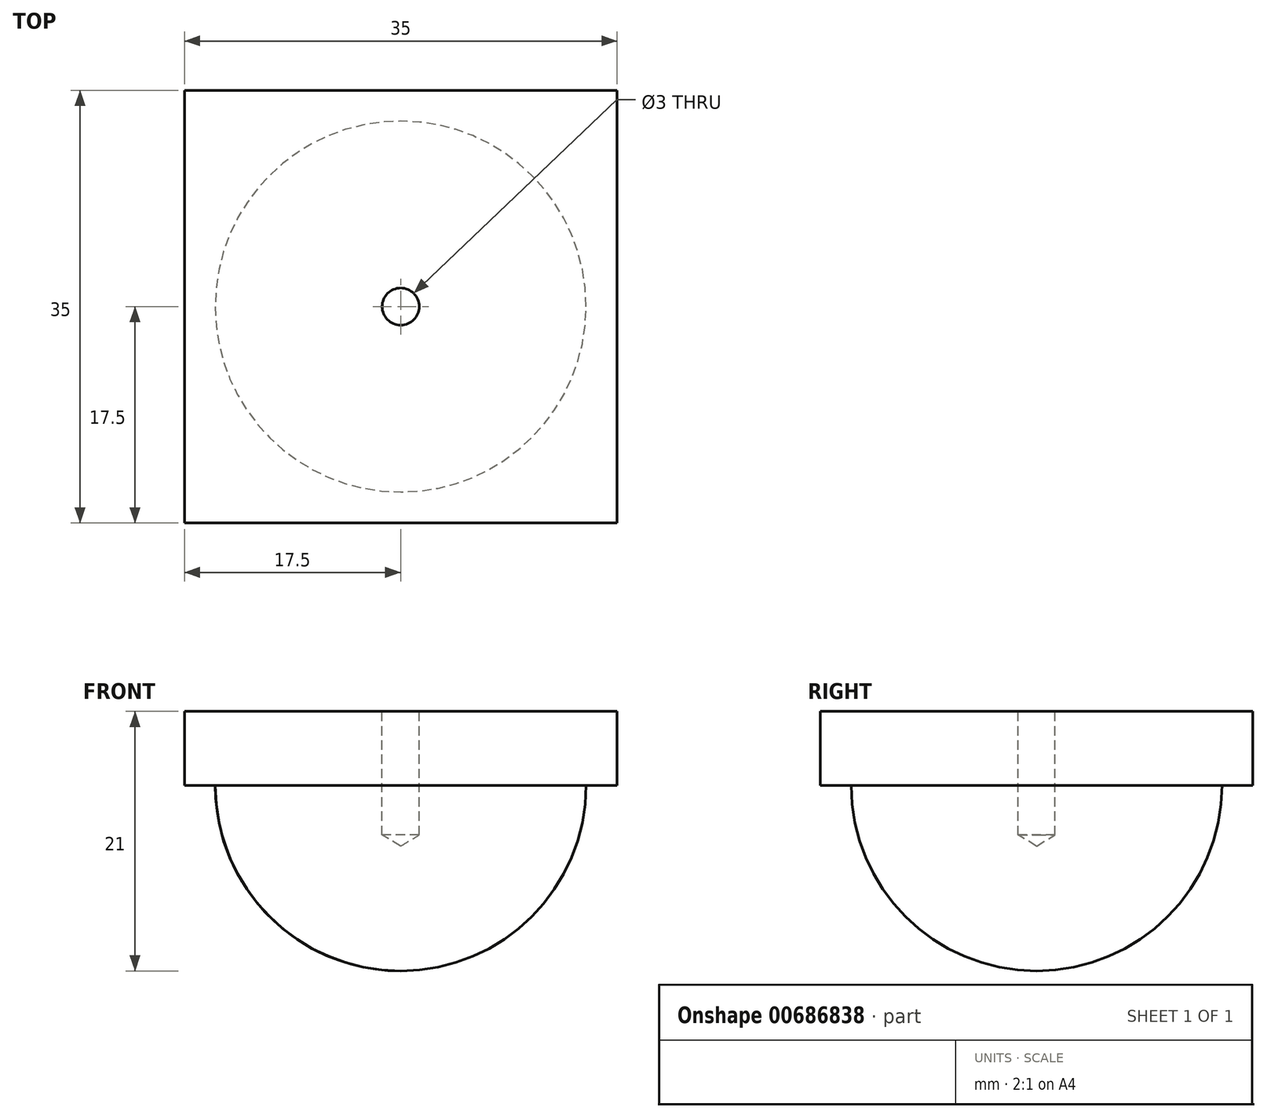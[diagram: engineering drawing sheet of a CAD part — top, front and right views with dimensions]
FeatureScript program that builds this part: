
annotation { "Feature Type Name" : "Feature", "Feature Type Description" : "" }
export const myFeature = defineFeature(function(context is Context, id is Id, definition is map)
    precondition{}
    {
        {
            var Q0;
            Q0=qCreatedBy(makeId("Top.planeOp"),FACE);
            var sketch = newSketch(context, id + "F0", { "sketchPlane" : qUnion([Q0])});
            skLineSegment(sketch, "E0.bottom", {"start": v(-17.5, -17.5) * mm, "end": v(17.5, -17.5) * mm});
            skLineSegment(sketch, "E0.top", {"start": v(-17.5, 17.5) * mm, "end": v(17.5, 17.5) * mm});
            skLineSegment(sketch, "E0.left", {"start": v(-17.5, -17.5) * mm, "end": v(-17.5, 17.5) * mm});
            skLineSegment(sketch, "E0.right", {"start": v(17.5, -17.5) * mm, "end": v(17.5, 17.5) * mm});
            skPoint(sketch, "E0.middle", {"position": v(0, 0) * mm});
            skSolve(sketch);
        }
        {
            var Q0;
            Q0 = qSketchRegion(id + "F0", true);
            extrude(context, id + "F1", {"entities" : qUnion([Q0]), "oppositeDirection" : true, "depth" : 6 * mm, "offsetDistance" : 25 * mm});
        }
        {
            var Q0;
            Q0=qCreatedBy(makeId("Front.planeOp"),FACE);
            var sketch = newSketch(context, id + "F2", { "sketchPlane" : qUnion([Q0])});
            skPoint(sketch, "E1.0", {"position": v(0, -6) * mm});
            skArc(sketch, "E2", {"start": v(0, -21) * mm, "mid": v(10.6, -16.6) * mm, "end": v(15, -6) * mm});
            skLineSegment(sketch, "E3.0", {"start": v(0, -6) * mm, "end": v(15, -6) * mm});
            skPoint(sketch, "E4", {"position": v(15, -6) * mm});
            skLineSegment(sketch, "E5", {"start": v(0, -6) * mm, "end": v(0, -21) * mm});
            skSolve(sketch);
        }
        {
            var Q0;
            Q0 = qSketchRegion(id + "F2", true);
            var Q1;
            Q1=sQuery(id+"F2.wireOp",EDGE,"E5");
            revolve(context, id + "F3", {"operationType" : NewBodyOperationType.ADD, "surfaceOperationType" : NewSurfaceOperationType.NEW, "entities" : qUnion([Q0]), "axis" : qUnion([Q1]), "revolveType" : RevolveType.FULL});
        }
        {
            var Q0;
            Q0=sQuery(id+"F0.wireOp",VERTEX,"E0.middle");
            var Q1;
            Q1=makeQuery(id+"F1.opExtrude","SWEPT_BODY",BODY,{"disambiguationData":[OSD([sQuery(id+"F0.wireOp",EDGE,"E0.bottom"),sQuery(id+"F0.wireOp",EDGE,"E0.top"),sQuery(id+"F0.wireOp",EDGE,"E0.left"),sQuery(id+"F0.wireOp",EDGE,"E0.right")])]});
            hole(context, id + "F4", {"style" : HoleStyle.SIMPLE, "endStyle" : HoleEndStyle.BLIND, "standardTappedOrClearance" : lookupTablePath({ "standard" : "ISO", "size" : "3", "type" : "Drilled" }), "standardBlindInLast" : lookupTablePath({ "standard" : "ISO", "size" : "3", "type" : "Drilled" }), "holeDiameter" : 3 * mm, "majorDiameter" : 5 * mm, "holeDepth" : 10 * mm, "tappedDepth" : 15 * mm, "tapClearance" : 3, "locations" : qUnion([Q0]), "scope" : qUnion([Q1])});
        }
    });
